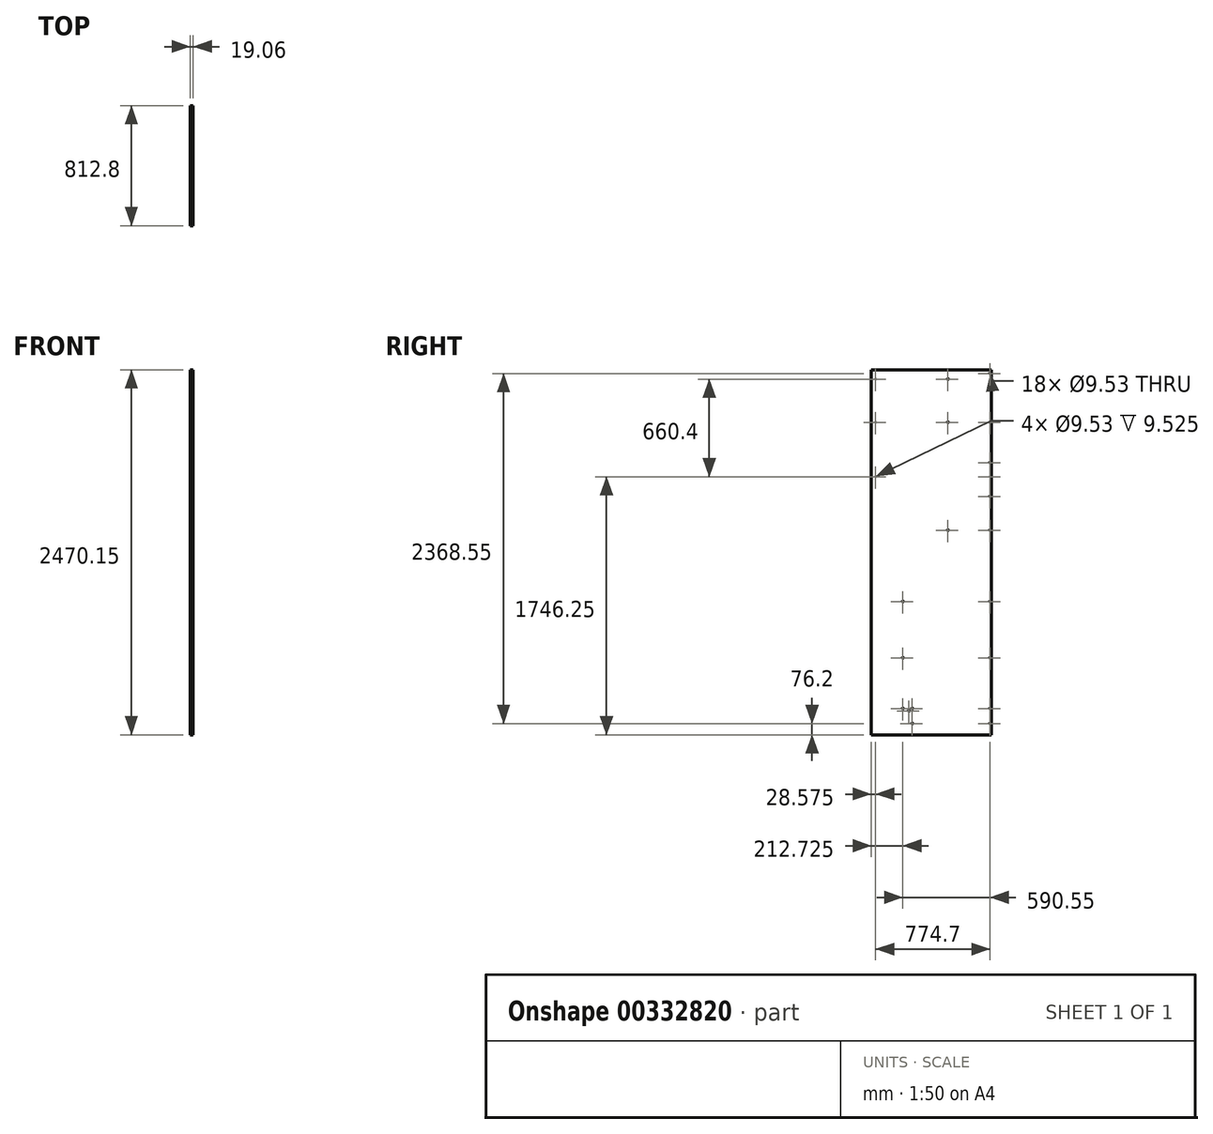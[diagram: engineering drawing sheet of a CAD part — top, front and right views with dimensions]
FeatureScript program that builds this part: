
annotation { "Feature Type Name" : "Feature", "Feature Type Description" : "" }
export const myFeature = defineFeature(function(context is Context, id is Id, definition is map)
    precondition{}
    {
        {
            var Q0;
            Q0=qCreatedBy(makeId("Right.planeOp"),FACE);
            var sketch = newSketch(context, id + "F0", { "sketchPlane" : qUnion([Q0])});
            skLineSegment(sketch, "E0.bottom", {"start": v(0, 0) * mm, "end": v(-812.8, 0) * mm});
            skLineSegment(sketch, "E0.top", {"start": v(0, 2470.15) * mm, "end": v(-812.8, 2470.15) * mm});
            skLineSegment(sketch, "E0.left", {"start": v(0, 0) * mm, "end": v(0, 2470.15) * mm});
            skLineSegment(sketch, "E0.right", {"start": v(-812.8, 0) * mm, "end": v(-812.8, 2470.15) * mm});
            skSolve(sketch);
        }
        {
            var Q0;
            Q0 = qSketchRegion(id + "F0", true);
            extrude(context, id + "F1", {"entities" : qUnion([Q0]), "endBound" : BoundingType.SYMMETRIC, "depth" : 19.05 * mm});
        }
        {
            var Q0;
            Q0=qCreatedBy(makeId("Right.planeOp"),FACE);
            var sketch = newSketch(context, id + "F2", { "sketchPlane" : qUnion([Q0])});
            skCircle(sketch, "E1", {"center": v(-295.28, 1384.3) * mm, "radius": 4.76 * mm});
            skCircle(sketch, "E2", {"center": v(-295.27, 2114.55) * mm, "radius": 4.76 * mm});
            skCircle(sketch, "E3", {"center": v(-295.28, 2406.65) * mm, "radius": 4.76 * mm});
            skCircle(sketch, "E4", {"center": v(-9.53, 2444.75) * mm, "radius": 4.76 * mm});
            skCircle(sketch, "E5", {"center": v(-9.53, 2114.55) * mm, "radius": 4.76 * mm});
            skCircle(sketch, "E6", {"center": v(-9.53, 1384.3) * mm, "radius": 4.76 * mm});
            skCircle(sketch, "E7", {"center": v(-9.53, 1612.9) * mm, "radius": 4.76 * mm});
            skCircle(sketch, "E8", {"center": v(-9.53, 1841.5) * mm, "radius": 4.76 * mm});
            skCircle(sketch, "E9", {"center": v(-9.53, 76.2) * mm, "radius": 4.76 * mm});
            skCircle(sketch, "E10", {"center": v(-9.53, 177.8) * mm, "radius": 4.76 * mm});
            skCircle(sketch, "E11", {"center": v(-9.53, 520.7) * mm, "radius": 4.76 * mm});
            skCircle(sketch, "E12", {"center": v(-9.53, 901.7) * mm, "radius": 4.76 * mm});
            skCircle(sketch, "E13", {"center": v(-536.58, 76.2) * mm, "radius": 4.76 * mm});
            skCircle(sketch, "E14", {"center": v(-536.58, 177.8) * mm, "radius": 4.76 * mm});
            skCircle(sketch, "E15", {"center": v(-600.08, 177.8) * mm, "radius": 4.76 * mm});
            skCircle(sketch, "E16", {"center": v(-558.8, 161.93) * mm, "radius": 4.76 * mm});
            skCircle(sketch, "E17", {"center": v(-600.08, 520.7) * mm, "radius": 4.76 * mm});
            skCircle(sketch, "E18", {"center": v(-600.08, 901.7) * mm, "radius": 4.76 * mm});
            skSolve(sketch);
        }
        {
            var Q0;
            Q0 = qSketchRegion(id + "F2", true);
            extrude(context, id + "F3", {"entities" : qUnion([Q0]), "operationType" : NewBodyOperationType.REMOVE, "endBound" : BoundingType.SYMMETRIC, "depth" : 25.4 * mm});
        }
        {
            var Q0;
            Q0=qCreatedBy(makeId("Right.planeOp"),FACE);
            var sketch = newSketch(context, id + "F4", { "sketchPlane" : qUnion([Q0])});
            skCircle(sketch, "E19", {"center": v(-784.23, 1746.25) * mm, "radius": 4.76 * mm});
            skCircle(sketch, "E20", {"center": v(-784.23, 2114.55) * mm, "radius": 4.76 * mm});
            skCircle(sketch, "E21", {"center": v(-784.23, 2406.65) * mm, "radius": 4.76 * mm});
            skCircle(sketch, "E22", {"center": v(-9.53, 1746.25) * mm, "radius": 4.76 * mm});
            skSolve(sketch);
        }
        {
            var Q0;
            Q0 = qSketchRegion(id + "F4", true);
            extrude(context, id + "F5", {"entities" : qUnion([Q0]), "operationType" : NewBodyOperationType.REMOVE, "oppositeDirection" : true, "depth" : 25.4 * mm});
        }
    });
